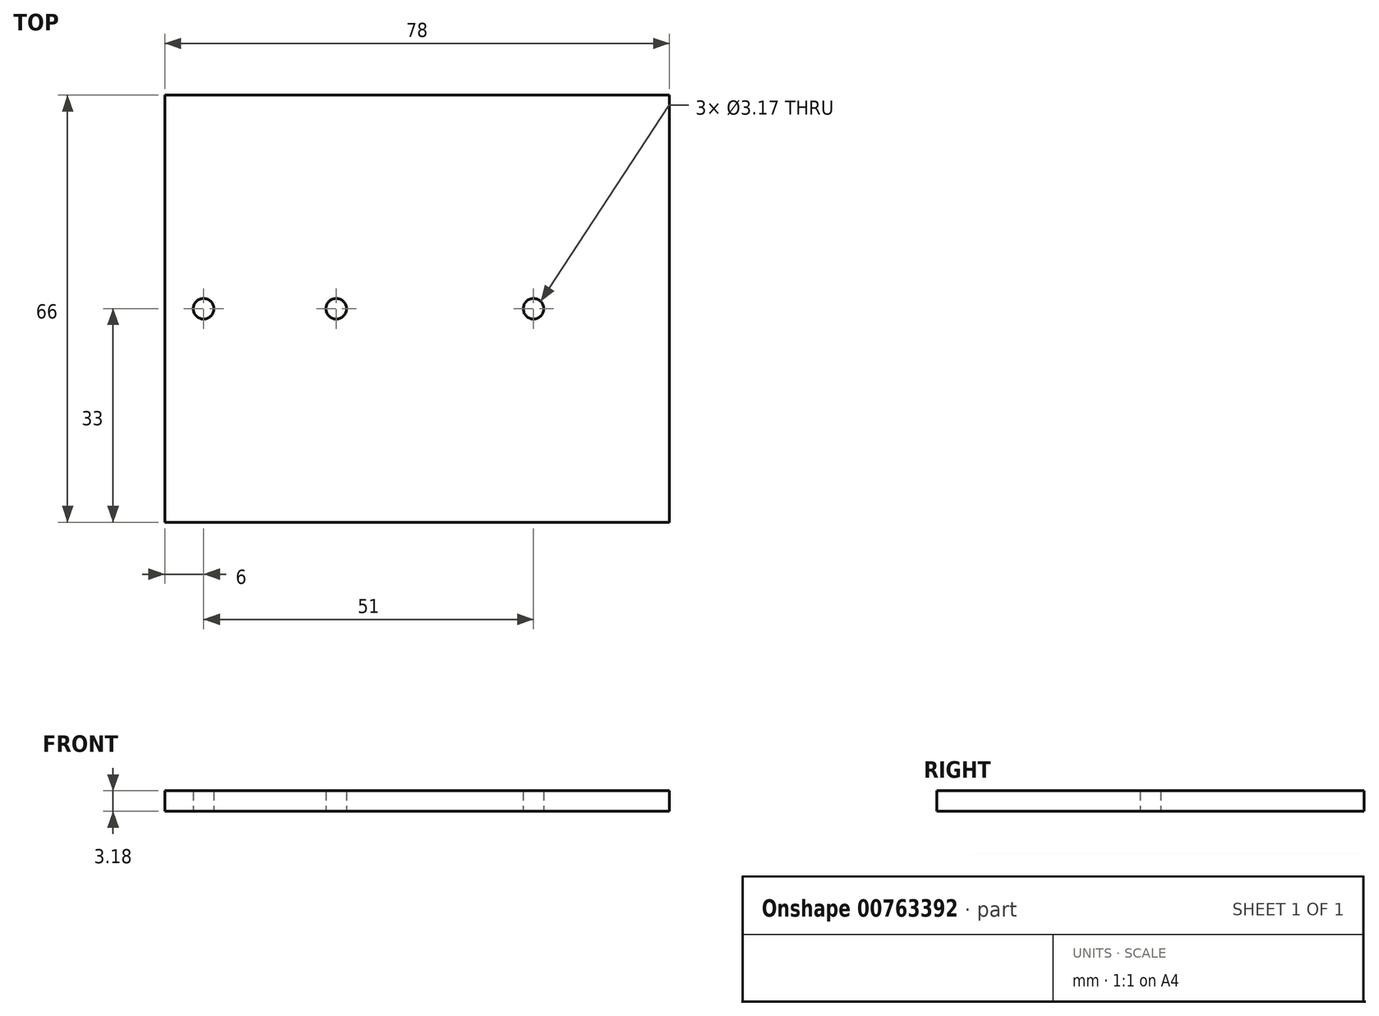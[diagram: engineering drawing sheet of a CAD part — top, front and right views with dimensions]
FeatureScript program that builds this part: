
annotation { "Feature Type Name" : "Feature", "Feature Type Description" : "" }
export const myFeature = defineFeature(function(context is Context, id is Id, definition is map)
    precondition{}
    {
        {
            var Q0;
            Q0=qCreatedBy(makeId("Top.planeOp"),FACE);
            var sketch = newSketch(context, id + "F0", { "sketchPlane" : qUnion([Q0])});
            skLineSegment(sketch, "E0.bottom", {"start": v(0, 0) * mm, "end": v(78, 0) * mm});
            skLineSegment(sketch, "E0.top", {"start": v(0, 66) * mm, "end": v(78, 66) * mm});
            skLineSegment(sketch, "E0.left", {"start": v(0, 0) * mm, "end": v(0, 66) * mm});
            skLineSegment(sketch, "E0.right", {"start": v(78, 0) * mm, "end": v(78, 66) * mm});
            skPoint(sketch, "E1", {"position": v(6, 33) * mm});
            skPoint(sketch, "E2", {"position": v(57, 33) * mm});
            skPoint(sketch, "E3", {"position": v(26.5, 33) * mm});
            skCircle(sketch, "E4", {"center": v(26.5, 33) * mm, "radius": 1.59 * mm});
            skCircle(sketch, "E5", {"center": v(57, 33) * mm, "radius": 1.59 * mm});
            skCircle(sketch, "E6", {"center": v(6, 33) * mm, "radius": 1.59 * mm});
            skPoint(sketch, "E7", {"position": v(0, 33) * mm});
            skSolve(sketch);
        }
        {
            var Q0;
            Q0=makeQuery(id+"F0.imprint","IMPRINT",FACE,{"disambiguationData":[TD([[makeQuery(id+"F0.imprint","IMPRINT",EDGE,{"derivedFrom":sQuery(id+"F0.wireOp",EDGE,"E0.bottom")}),1.0]])]});
            extrude(context, id + "F1", {"entities" : qUnion([Q0]), "depth" : 3.17 * mm, "offsetDistance" : 25.4 * mm});
        }
    });
